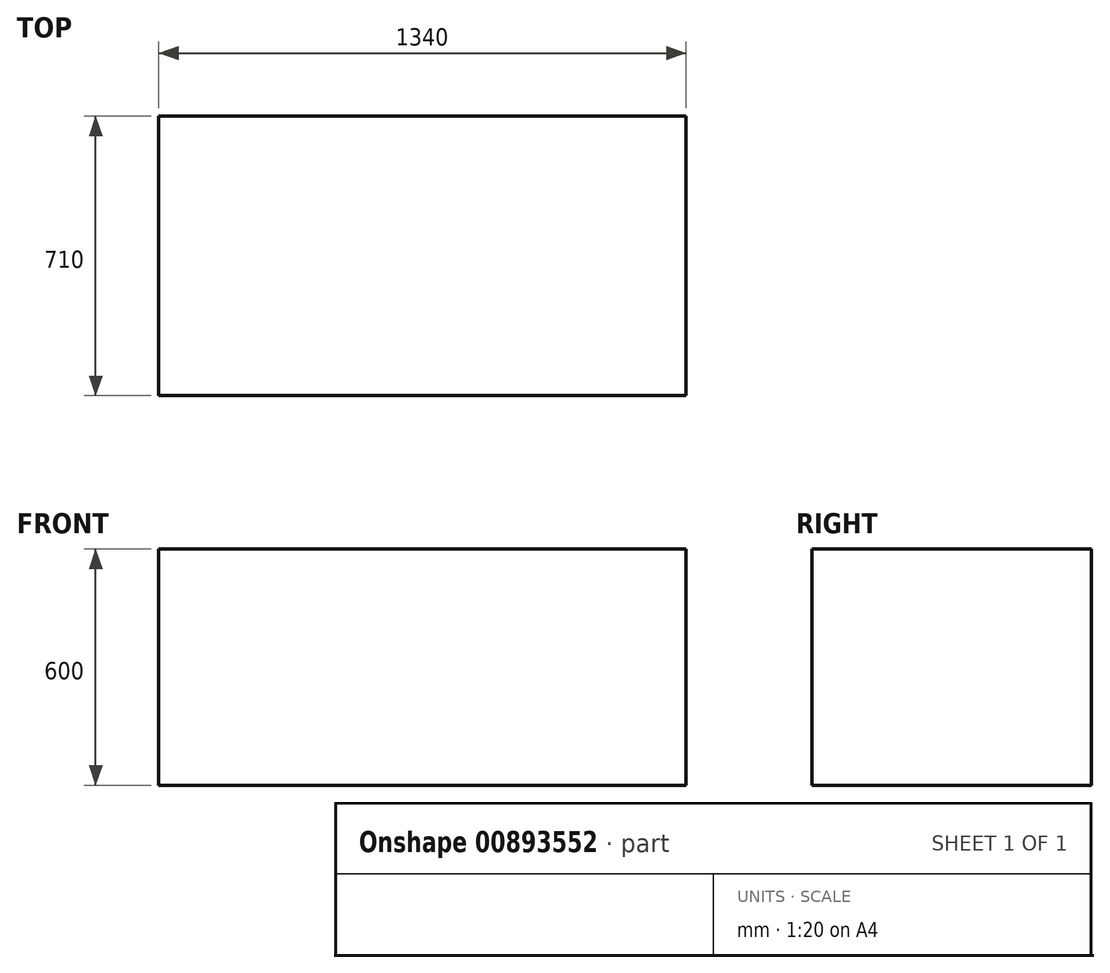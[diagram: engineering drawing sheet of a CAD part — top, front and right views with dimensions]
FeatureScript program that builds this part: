
annotation { "Feature Type Name" : "Feature", "Feature Type Description" : "" }
export const myFeature = defineFeature(function(context is Context, id is Id, definition is map)
    precondition{}
    {
        {
            var Q0;
            Q0=qCreatedBy(makeId("Top.planeOp"),FACE);
            var sketch = newSketch(context, id + "F0", { "sketchPlane" : qUnion([Q0])});
            skLineSegment(sketch, "E0.bottom", {"start": v(670, -355) * mm, "end": v(-670, -355) * mm});
            skLineSegment(sketch, "E0.top", {"start": v(670, 355) * mm, "end": v(-670, 355) * mm});
            skLineSegment(sketch, "E0.left", {"start": v(670, -355) * mm, "end": v(670, 355) * mm});
            skLineSegment(sketch, "E0.right", {"start": v(-670, -355) * mm, "end": v(-670, 355) * mm});
            skPoint(sketch, "E0.middle", {"position": v(0, 0) * mm});
            skSolve(sketch);
        }
        {
            var Q0;
            Q0 = qSketchRegion(id + "F0", true);
            extrude(context, id + "F1", {"entities" : qUnion([Q0]), "endBound" : BoundingType.SYMMETRIC, "depth" : 600 * mm, "offsetDistance" : 25 * mm});
        }
    });
